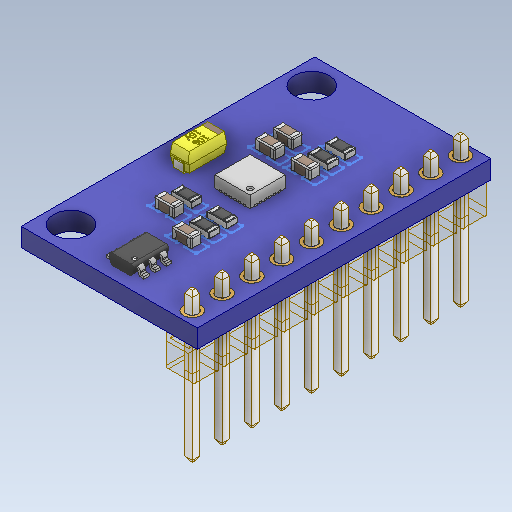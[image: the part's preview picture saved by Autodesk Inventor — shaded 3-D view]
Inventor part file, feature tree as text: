
AUTODESK INVENTOR PART (.ipt)
format: ipt  version: 2020.3 (Build 243373000, 373)  size: 1,635,840 bytes
history: native  units: in
note: dims shown in document units (in); Inventor stores cm internally (conversion verified against a paired STEP export)
features: other x37, hole x20, sketch x10
ambient origin geometry x8: Origin, YZ Plane, XZ Plane, XY Plane, X Axis, Y Axis, Z Axis, Center Point
bodies: Solid1 (feature_tree), Solid2 (feature_tree), Solid3 (feature_tree), Solid4 (feature_tree), Solid5 (feature_tree), Solid6 (feature_tree), Solid7 (feature_tree), Solid8 (feature_tree), Solid9 (feature_tree), Solid10 (feature_tree), Solid11 (feature_tree), Solid12 (feature_tree), Solid13 (feature_tree), Solid14 (feature_tree), Solid15 (feature_tree), Solid16 (feature_tree), Solid17 (feature_tree), Solid18 (feature_tree), Solid19 (feature_tree), Solid20 (feature_tree), Solid21 (feature_tree), Solid22 (feature_tree), Solid23 (feature_tree), Solid24 (feature_tree), Solid25 (feature_tree), Solid26 (feature_tree), Solid27 (feature_tree), Solid28 (feature_tree), Solid29 (feature_tree), Solid30 (feature_tree), Solid31 (feature_tree), Solid32 (feature_tree), Solid33 (feature_tree), Solid34 (feature_tree), Solid35 (feature_tree), Solid36 (feature_tree), Solid37 (feature_tree), Solid38 (feature_tree), Solid39 (feature_tree), Solid40 (feature_tree), Solid41 (feature_tree), Solid42 (feature_tree), Solid43 (feature_tree), Solid44 (feature_tree), Solid45 (feature_tree), Solid46 (feature_tree), Solid47 (feature_tree), Solid48 (feature_tree), Solid49 (feature_tree), Solid50 (feature_tree), Solid51 (feature_tree), Solid52 (feature_tree), Solid53 (feature_tree), Solid54 (feature_tree)
feature tree (67):
  other  "Repaired Geometry1"
  sketch  "3D Sketch1"
  sketch  "3D Sketch2"
  sketch  "3D Sketch3"
  sketch  "3D Sketch4"
  sketch  "3D Sketch5"
  sketch  "3D Sketch6"
  sketch  "3D Sketch7"
  sketch  "3D Sketch8"
  sketch  "3D Sketch9"
  sketch  "3D Sketch10"
  other  "board_1:1"
  hole  "hole_plating_1:1"  [1 undecoded]
  hole  "hole_plating_2:1"  [1 undecoded]
  hole  "hole_plating_3:1"  [1 undecoded]
  hole  "hole_plating_4:1"  [1 undecoded]
  hole  "hole_plating_5:1"  [1 undecoded]
  hole  "hole_plating_6:1"  [1 undecoded]
  hole  "hole_plating_7:1"  [1 undecoded]
  hole  "hole_plating_8:1"  [1 undecoded]
  hole  "hole_plating_9:1"  [1 undecoded]
  hole  "hole_plating_10:1"  [1 undecoded]
  hole  "hole_plating_11:1"  [1 undecoded]
  hole  "hole_plating_12:1"  [1 undecoded]
  hole  "hole_plating_13:1"  [1 undecoded]
  hole  "hole_plating_14:1"  [1 undecoded]
  hole  "hole_plating_15:1"  [1 undecoded]
  hole  "hole_plating_16:1"  [1 undecoded]
  hole  "hole_plating_17:1"  [1 undecoded]
  hole  "hole_plating_18:1"  [1 undecoded]
  hole  "hole_plating_19:1"  [1 undecoded]
  hole  "hole_plating_20:1"  [1 undecoded]
  other  "Pin Header 1x10 TH Pitch 2.54mm_1:1"
  other  "Pin Header 1x10 TH Pitch 2.54mm_1:2"
  other  "Pin Header 1x10 TH Pitch 2.54mm_1:3"
  other  "Pin Header 1x10 TH Pitch 2.54mm_1:4"
  other  "Pin Header 1x10 TH Pitch 2.54mm_1:5"
  other  "Pin Header 1x10 TH Pitch 2.54mm_1:6"
  other  "Pin Header 1x10 TH Pitch 2.54mm_1:7"
  other  "Pin Header 1x10 TH Pitch 2.54mm_1:8"
  other  "Pin Header 1x10 TH Pitch 2.54mm_1:9"
  other  "Pin Header 1x10 TH Pitch 2.54mm_1:10"
  other  "MPU-9250_1:1"
  other  "tantalum 10uF_1:1"
  other  "SOT23_5_1:1"
  other  "RESC-0603_1:1"
  other  "RESC-0603_1:2"
  other  "RESC-0603_1:3"
  other  "RESC-0603_2:1"
  other  "RESC-0603_2:2"
  other  "RESC-0603_2:3"
  other  "RESC-0603_3:1"
  other  "RESC-0603_3:2"
  other  "RESC-0603_3:3"
  other  "RESC-0603_4:1"
  other  "RESC-0603_4:2"
  other  "RESC-0603_4:3"
  other  "RESC-0603_5:1"
  other  "RESC-0603_5:2"
  other  "RESC-0603_5:3"
  other  "CAPC-0603-T0.9-BN_1:1"
  other  "CAPC-0603-T0.9-BN_2:1"
  other  "CAPC-0603-T0.9-BN_3:1"
  other  "CAPC-0603-T0.9-BN_4:1"
  other  "CAPC-0603-T0.9-BN_5:1"
  other  "Composite1"
  other  "Srf1"
note: 20 required parameter values undecoded (feature->parameter linkage not recoverable at this tier; creation-order binding heuristic only, values carry confidence <= 0.55)
